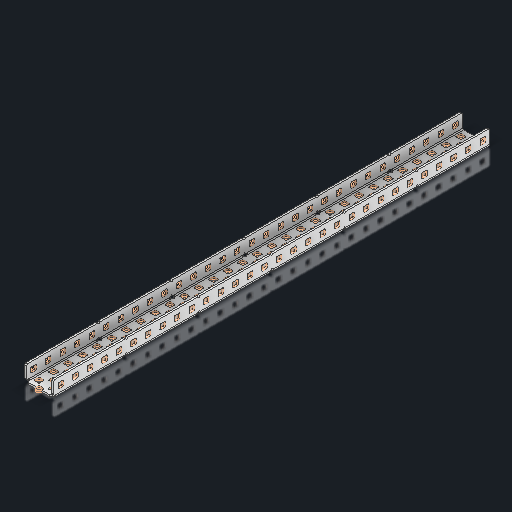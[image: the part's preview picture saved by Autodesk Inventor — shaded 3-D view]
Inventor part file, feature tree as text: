
AUTODESK INVENTOR PART (.ipt)
format: ipt  version: 2023.2 (Build 272271030, 271C)  size: 2,567,680 bytes
history: native  units: in
note: dims shown in document units (in); Inventor stores cm internally (conversion verified against a paired STEP export)
features: other x306, sketch x10, sheet_metal_op x1
ambient origin geometry x8: Origin, YZ Plane, XZ Plane, XY Plane, X Axis, Y Axis, Z Axis, Center Point
bodies: Solid1 (feature_tree)
feature tree (317):
  other  "Alu C 1x2x1x30_MIR_MIR.ipt"
  other  "Solid1::Alu C 1x2x1x30_MIR_MIR.ipt"
  other  "TaggingFeature1"
  sketch  "Sketch1"  dims[d0=0.3937in]
  sketch  "Sketch2"  dims[d1=0.0625in]
  sketch  "Sketch3"
  sketch  "Sketch7"
  other  "Flange Pattern Sketch"
  sketch  "Sketch8"
  sketch  "Sketch9"
  sheet_metal_op  "Body Pattern Sketch"
  sketch  "Sketch15"
  sketch  "Sketch16"
  other  "Arc Length"
  sketch  "Sketch13"
  sketch  "Sketch14"
  other  "Flange Pattern Plane"
  other  "Srf1"
  other  "Srf2"
  other  "Srf3"
  other  "Srf4"
  other  "Srf5"
  other  "Srf6"
  other  "Srf7"
  other  "Srf8"
  other  "Srf9"
  other  "Srf10"
  other  "Srf11"
  other  "Srf12"
  other  "Srf13"
  other  "Srf14"
  other  "Srf15"
  other  "Srf16"
  other  "Srf17"
  other  "Srf18"
  other  "Srf19"
  other  "Srf20"
  other  "Srf21"
  other  "Srf22"
  other  "Srf23"
  other  "Srf24"
  other  "Srf25"
  other  "Srf26"
  other  "Srf27"
  other  "Srf28"
  other  "Srf29"
  other  "Srf30"
  other  "Srf31"
  other  "Srf32"
  other  "Srf33"
  other  "Srf34"
  other  "Srf35"
  other  "Srf36"
  other  "Srf37"
  other  "Srf38"
  other  "Srf39"
  other  "Srf40"
  other  "Srf41"
  other  "Srf42"
  other  "Srf43"
  other  "Srf44"
  other  "Srf45"
  other  "Srf46"
  other  "Srf47"
  other  "Srf48"
  other  "Srf49"
  other  "Srf50"
  other  "Srf51"
  other  "Srf52"
  other  "Srf53"
  other  "Srf54"
  other  "Srf55"
  other  "Srf56"
  other  "Srf57"
  other  "Srf58"
  other  "Srf59"
  other  "Srf60"
  other  "Srf61"
  other  "Srf62"
  other  "Srf63"
  other  "Srf64"
  other  "Srf65"
  other  "Srf66"
  other  "Srf67"
  other  "Srf68"
  other  "Srf69"
  other  "Srf70"
  other  "Srf71"
  other  "Srf72"
  other  "Srf73"
  other  "Srf74"
  other  "Srf75"
  other  "Srf76"
  other  "Srf77"
  other  "Srf78"
  other  "Srf79"
  other  "Srf80"
  other  "Srf81"
  other  "Srf82"
  other  "Srf83"
  other  "Srf84"
  other  "Srf85"
  other  "Srf86"
  other  "Srf87"
  other  "Srf88"
  other  "Srf89"
  other  "Srf90"
  other  "Srf91"
  other  "Srf92"
  other  "Srf93"
  other  "Srf94"
  other  "Srf95"
  other  "Srf96"
  other  "Srf97"
  other  "Srf98"
  other  "Srf99"
  other  "Srf100"
  other  "Srf101"
  other  "Srf102"
  other  "Srf103"
  other  "Srf104"
  other  "Srf105"
  other  "Srf106"
  other  "Srf107"
  other  "Srf108"
  other  "Srf109"
  other  "Srf110"
  other  "Srf111"
  other  "Srf112"
  other  "Srf113"
  other  "Srf114"
  other  "Srf115"
  other  "Srf116"
  other  "Srf117"
  other  "Srf118"
  other  "Srf119"
  other  "Srf120"
  other  "Srf121"
  other  "Srf122"
  other  "Srf123"
  other  "Srf124"
  other  "Srf125"
  other  "Srf126"
  other  "Srf127"
  other  "Srf128"
  other  "Srf129"
  other  "Srf130"
  other  "Srf131"
  other  "Srf132"
  other  "Srf133"
  other  "Srf134"
  other  "Srf135"
  other  "Srf136"
  other  "Srf137"
  other  "Srf138"
  other  "Srf139"
  other  "Srf140"
  other  "Srf141"
  other  "Srf142"
  other  "Srf143"
  other  "Srf144"
  other  "Srf145"
  other  "Srf146"
  other  "Srf147"
  other  "Srf148"
  other  "Srf149"
  other  "Srf150"
  other  "Srf1::Derived"
  other  "Srf2::Derived"
  other  "Srf3::Derived"
  other  "Srf4::Derived"
  other  "Srf5::Derived"
  other  "Srf6::Derived"
  other  "Srf7::Derived"
  other  "Srf8::Derived"
  other  "Srf9::Derived"
  other  "Srf10::Derived"
  other  "Srf11::Derived"
  other  "Srf12::Derived"
  other  "Srf13::Derived"
  other  "Srf14::Derived"
  other  "Srf15::Derived"
  other  "Srf16::Derived"
  other  "Srf17::Derived"
  other  "Srf18::Derived"
  other  "Srf19::Derived"
  other  "Srf20::Derived"
  other  "Srf21::Derived"
  other  "Srf22::Derived"
  other  "Srf23::Derived"
  other  "Srf24::Derived"
  other  "Srf25::Derived"
  other  "Srf26::Derived"
  other  "Srf27::Derived"
  other  "Srf28::Derived"
  other  "Srf29::Derived"
  other  "Srf30::Derived"
  other  "Srf31::Derived"
  other  "Srf32::Derived"
  other  "Srf33::Derived"
  other  "Srf34::Derived"
  other  "Srf35::Derived"
  other  "Srf36::Derived"
  other  "Srf37::Derived"
  other  "Srf38::Derived"
  other  "Srf39::Derived"
  other  "Srf40::Derived"
  other  "Srf41::Derived"
  other  "Srf42::Derived"
  other  "Srf43::Derived"
  other  "Srf44::Derived"
  other  "Srf45::Derived"
  other  "Srf46::Derived"
  other  "Srf47::Derived"
  other  "Srf48::Derived"
  other  "Srf49::Derived"
  other  "Srf50::Derived"
  other  "Srf51::Derived"
  other  "Srf52::Derived"
  other  "Srf53::Derived"
  other  "Srf54::Derived"
  other  "Srf55::Derived"
  other  "Srf56::Derived"
  other  "Srf57::Derived"
  other  "Srf58::Derived"
  other  "Srf59::Derived"
  other  "Srf60::Derived"
  other  "Srf61::Derived"
  other  "Srf62::Derived"
  other  "Srf63::Derived"
  other  "Srf64::Derived"
  other  "Srf65::Derived"
  other  "Srf66::Derived"
  other  "Srf67::Derived"
  other  "Srf68::Derived"
  other  "Srf69::Derived"
  other  "Srf70::Derived"
  other  "Srf71::Derived"
  other  "Srf72::Derived"
  other  "Srf73::Derived"
  other  "Srf74::Derived"
  other  "Srf75::Derived"
  other  "Srf76::Derived"
  other  "Srf77::Derived"
  other  "Srf78::Derived"
  other  "Srf79::Derived"
  other  "Srf80::Derived"
  other  "Srf81::Derived"
  other  "Srf82::Derived"
  other  "Srf83::Derived"
  other  "Srf84::Derived"
  other  "Srf85::Derived"
  other  "Srf86::Derived"
  other  "Srf87::Derived"
  other  "Srf88::Derived"
  other  "Srf89::Derived"
  other  "Srf90::Derived"
  other  "Srf91::Derived"
  other  "Srf92::Derived"
  other  "Srf93::Derived"
  other  "Srf94::Derived"
  other  "Srf95::Derived"
  other  "Srf96::Derived"
  other  "Srf97::Derived"
  other  "Srf98::Derived"
  other  "Srf99::Derived"
  other  "Srf100::Derived"
  other  "Srf101::Derived"
  other  "Srf102::Derived"
  other  "Srf103::Derived"
  other  "Srf104::Derived"
  other  "Srf105::Derived"
  other  "Srf106::Derived"
  other  "Srf107::Derived"
  other  "Srf108::Derived"
  other  "Srf109::Derived"
  other  "Srf110::Derived"
  other  "Srf111::Derived"
  other  "Srf112::Derived"
  other  "Srf113::Derived"
  other  "Srf114::Derived"
  other  "Srf115::Derived"
  other  "Srf116::Derived"
  other  "Srf117::Derived"
  other  "Srf118::Derived"
  other  "Srf119::Derived"
  other  "Srf120::Derived"
  other  "Srf121::Derived"
  other  "Srf122::Derived"
  other  "Srf123::Derived"
  other  "Srf124::Derived"
  other  "Srf125::Derived"
  other  "Srf126::Derived"
  other  "Srf127::Derived"
  other  "Srf128::Derived"
  other  "Srf129::Derived"
  other  "Srf130::Derived"
  other  "Srf131::Derived"
  other  "Srf132::Derived"
  other  "Srf133::Derived"
  other  "Srf134::Derived"
  other  "Srf135::Derived"
  other  "Srf136::Derived"
  other  "Srf137::Derived"
  other  "Srf138::Derived"
  other  "Srf139::Derived"
  other  "Srf140::Derived"
  other  "Srf141::Derived"
  other  "Srf142::Derived"
  other  "Srf143::Derived"
  other  "Srf144::Derived"
  other  "Srf145::Derived"
  other  "Srf146::Derived"
  other  "Srf147::Derived"
  other  "Srf148::Derived"
  other  "Srf149::Derived"
  other  "Srf150::Derived"
